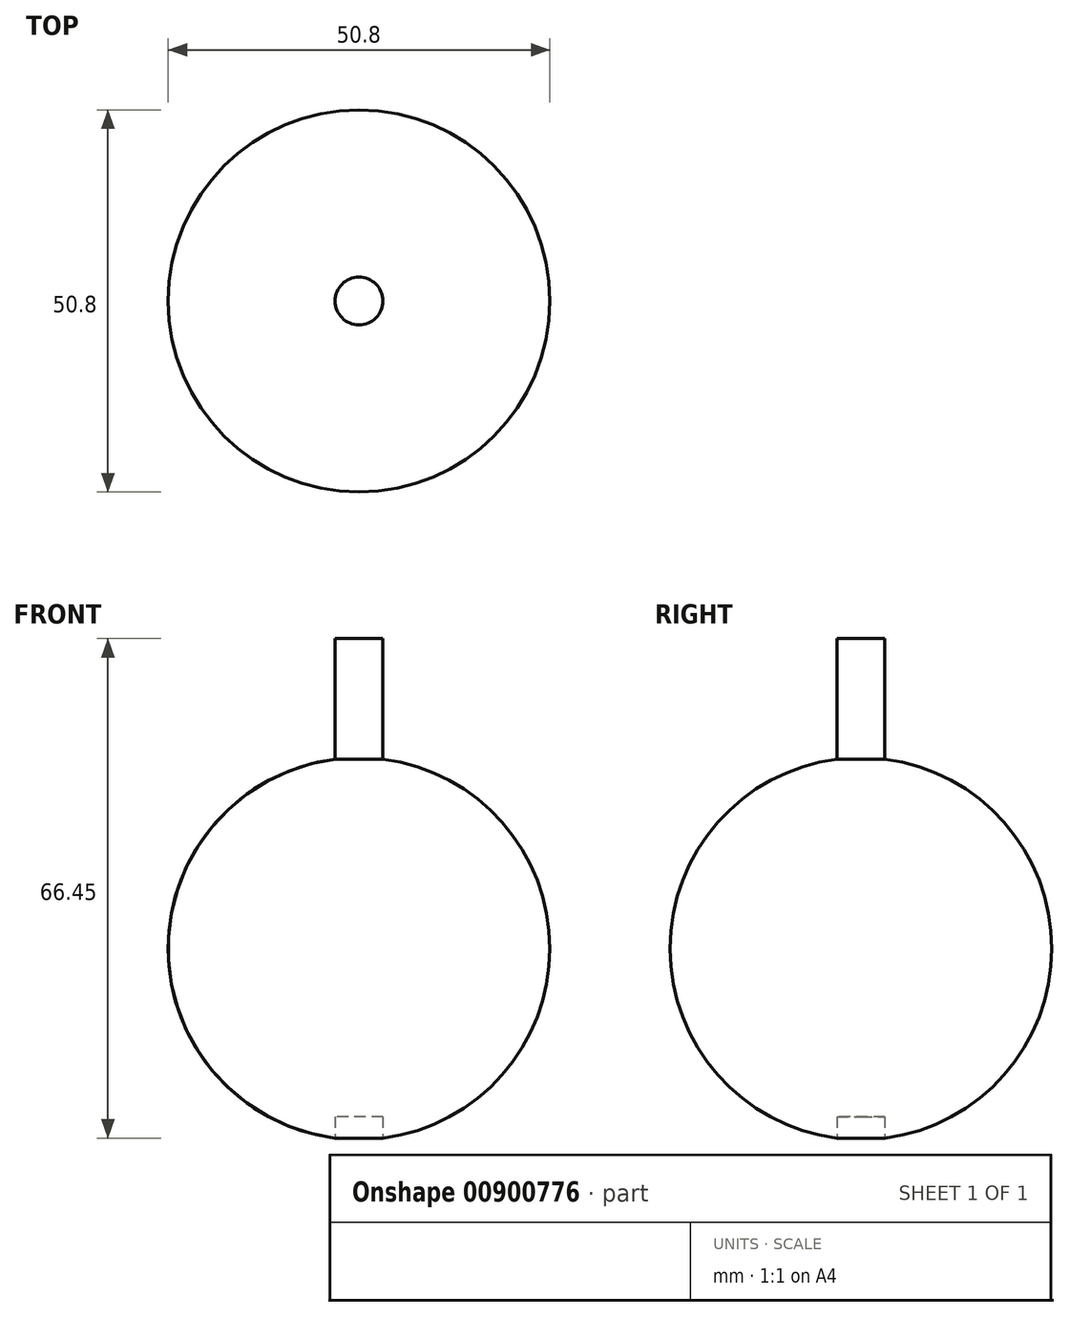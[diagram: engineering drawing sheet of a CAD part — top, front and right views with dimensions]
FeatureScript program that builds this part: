
annotation { "Feature Type Name" : "Feature", "Feature Type Description" : "" }
export const myFeature = defineFeature(function(context is Context, id is Id, definition is map)
    precondition{}
    {
        {
            var Q0;
            Q0=qCreatedBy(makeId("Front.planeOp"),FACE);
            var sketch = newSketch(context, id + "F0", { "sketchPlane" : qUnion([Q0])});
            skArc(sketch, "E0", {"start": v(-3.18, 25.2) * mm, "mid": v(-25.35, -1.6) * mm, "end": v(0, -25.4) * mm});
            skLineSegment(sketch, "E1", {"start": v(0, -25.4) * mm, "end": v(0, 41.25) * mm});
            skPoint(sketch, "E2.start.orphan", {"position": v(-25.4, 0) * mm});
            skLineSegment(sketch, "E3", {"start": v(-3.17, 25.2) * mm, "end": v(-3.17, 41.25) * mm});
            skLineSegment(sketch, "E4", {"start": v(-3.17, 41.25) * mm, "end": v(0, 41.25) * mm});
            skSolve(sketch);
        }
        {
            var Q0;
            Q0=makeQuery(id+"F0.imprint","IMPRINT",FACE,{"disambiguationData":[TD([[makeQuery(id+"F0.imprint","IMPRINT",EDGE,{"derivedFrom":sQuery(id+"F0.wireOp",EDGE,"E0")}),1.0]])]});
            var Q1;
            Q1=sQuery(id+"F0.wireOp",EDGE,"E1");
            revolve(context, id + "F1", {"surfaceOperationType" : NewSurfaceOperationType.NEW, "entities" : qUnion([Q0]), "axis" : qUnion([Q1]), "revolveType" : RevolveType.FULL});
        }
        {
            var Q0;
            Q0=qCreatedBy(makeId("Top.planeOp"),FACE);
            cPlane(context, id + "F2", {"entities" : qUnion([Q0]), "cplaneType" : CPlaneType.OFFSET, "offset" : 25.4 * mm, "oppositeDirection" : true, "width" : 152.4 * mm, "height" : 152.4 * mm});
        }
        {
            var Q0;
            Q0=qCreatedBy(id+"F2.planeOp",FACE);
            var sketch = newSketch(context, id + "F3", { "sketchPlane" : qUnion([Q0])});
            skCircle(sketch, "E5", {"center": v(0, 0) * mm, "radius": 3.18 * mm});
            skSolve(sketch);
        }
        {
            var Q0;
            Q0=makeQuery(id+"F3.imprint","IMPRINT",FACE,{"disambiguationData":[TD([[makeQuery(id+"F3.imprint","IMPRINT",EDGE,{"derivedFrom":sQuery(id+"F3.wireOp",EDGE,"E5")}),1.0]])]});
            extrude(context, id + "F4", {"entities" : qUnion([Q0]), "operationType" : NewBodyOperationType.REMOVE, "depth" : 3.05 * mm, "offsetDistance" : 25.4 * mm});
        }
    });
